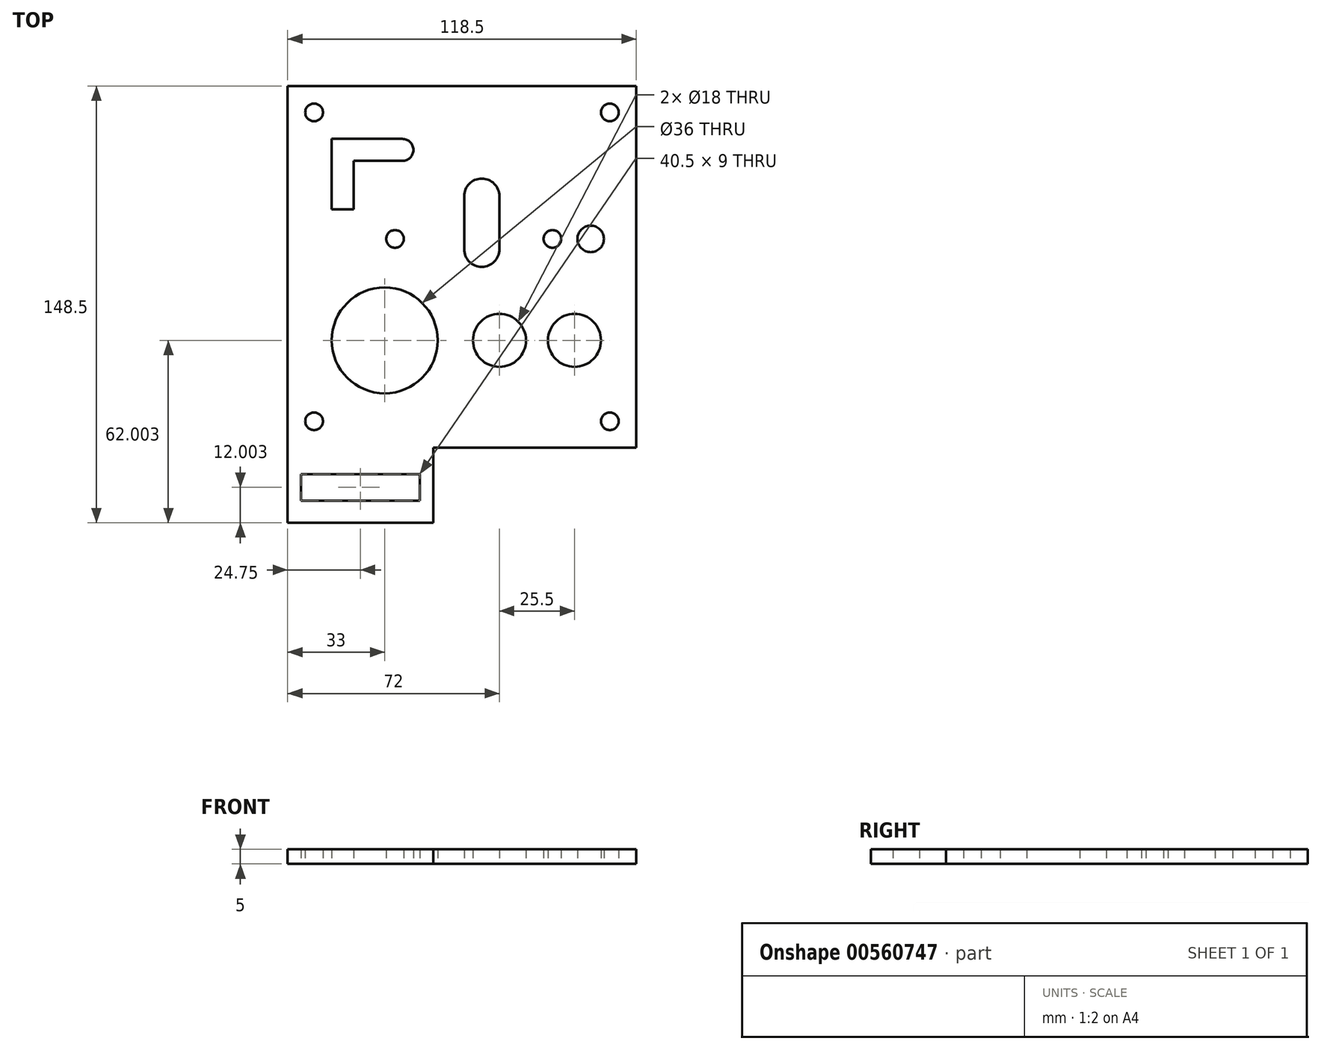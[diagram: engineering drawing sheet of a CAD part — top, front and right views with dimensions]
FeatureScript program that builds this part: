
annotation { "Feature Type Name" : "Feature", "Feature Type Description" : "" }
export const myFeature = defineFeature(function(context is Context, id is Id, definition is map)
    precondition{}
    {
        {
            var Q0;
            Q0=qCreatedBy(makeId("Top.planeOp"),FACE);
            var sketch = newSketch(context, id + "F0", { "sketchPlane" : qUnion([Q0])});
            skLineSegment(sketch, "E0", {"start": v(-66, 54.18) * mm, "end": v(52.5, 54.18) * mm});
            skLineSegment(sketch, "E1", {"start": v(52.5, 54.18) * mm, "end": v(52.5, -68.82) * mm});
            skLineSegment(sketch, "E2", {"start": v(-66, 54.18) * mm, "end": v(-66, -68.82) * mm});
            skLineSegment(sketch, "E3", {"start": v(-16.5, -68.82) * mm, "end": v(52.5, -68.82) * mm});
            skLineSegment(sketch, "E4", {"start": v(-66, 54.18) * mm, "end": v(-66, -94.32) * mm});
            skLineSegment(sketch, "E5", {"start": v(-66, -94.32) * mm, "end": v(-16.5, -94.32) * mm});
            skLineSegment(sketch, "E6", {"start": v(-16.5, -94.32) * mm, "end": v(-16.5, -68.82) * mm});
            skCircle(sketch, "E7", {"center": v(-57, 45.18) * mm, "radius": 3 * mm});
            skCircle(sketch, "E8", {"center": v(43.5, 45.18) * mm, "radius": 3 * mm});
            skCircle(sketch, "E9", {"center": v(43.5, -59.82) * mm, "radius": 3 * mm});
            skCircle(sketch, "E10", {"center": v(-57, -59.82) * mm, "radius": 3 * mm});
            skLineSegment(sketch, "E11.bottom", {"start": v(-61.5, -77.82) * mm, "end": v(-52.5, -77.82) * mm});
            skLineSegment(sketch, "E11.top", {"start": v(-61.5, -86.82) * mm, "end": v(-52.5, -86.82) * mm});
            skLineSegment(sketch, "E11.left", {"start": v(-61.5, -77.82) * mm, "end": v(-61.5, -86.82) * mm});
            skLineSegment(sketch, "E11.right", {"start": v(-52.5, -77.82) * mm, "end": v(-52.5, -86.82) * mm});
            skLineSegment(sketch, "E12.bottom", {"start": v(-45, -77.82) * mm, "end": v(-36, -77.82) * mm});
            skLineSegment(sketch, "E12.top", {"start": v(-45, -86.82) * mm, "end": v(-36, -86.82) * mm});
            skLineSegment(sketch, "E12.left", {"start": v(-45, -77.82) * mm, "end": v(-45, -86.82) * mm});
            skLineSegment(sketch, "E12.right", {"start": v(-36, -77.82) * mm, "end": v(-36, -86.82) * mm});
            skLineSegment(sketch, "E13.bottom", {"start": v(-30, -77.82) * mm, "end": v(-21, -77.82) * mm});
            skLineSegment(sketch, "E13.top", {"start": v(-30, -86.82) * mm, "end": v(-21, -86.82) * mm});
            skLineSegment(sketch, "E13.left", {"start": v(-30, -77.82) * mm, "end": v(-30, -86.82) * mm});
            skLineSegment(sketch, "E13.right", {"start": v(-21, -77.82) * mm, "end": v(-21, -86.82) * mm});
            skLineSegment(sketch, "E14", {"start": v(-61.5, -77.82) * mm, "end": v(-21, -77.82) * mm});
            skLineSegment(sketch, "E15", {"start": v(-61.5, -86.82) * mm, "end": v(-21, -86.82) * mm});
            skLineSegment(sketch, "E16", {"start": v(-51, 36.18) * mm, "end": v(-51, 12.18) * mm});
            skLineSegment(sketch, "E17", {"start": v(-51, 12.18) * mm, "end": v(-51, 36.18) * mm});
            skLineSegment(sketch, "E18", {"start": v(-51, 36.18) * mm, "end": v(-27, 36.18) * mm});
            skLineSegment(sketch, "E19", {"start": v(-51, 12.18) * mm, "end": v(-43.5, 12.18) * mm});
            skLineSegment(sketch, "E20", {"start": v(-43.5, 12.18) * mm, "end": v(-43.5, 28.68) * mm});
            skLineSegment(sketch, "E21", {"start": v(-43.5, 28.68) * mm, "end": v(-27, 28.68) * mm});
            skCircle(sketch, "E22", {"center": v(31.5, -32.32) * mm, "radius": 9 * mm});
            skCircle(sketch, "E23", {"center": v(6, -32.32) * mm, "radius": 9 * mm});
            skCircle(sketch, "E24", {"center": v(-33, -32.32) * mm, "radius": 18 * mm});
            skArc(sketch, "E25", {"start": v(-27, 28.68) * mm, "mid": v(-23.25, 32.43) * mm, "end": v(-27, 36.18) * mm});
            skLineSegment(sketch, "E26", {"start": v(-6, 16.68) * mm, "end": v(-6, -1.32) * mm});
            skLineSegment(sketch, "E27", {"start": v(6, -1.32) * mm, "end": v(6, 16.68) * mm});
            skArc(sketch, "E28", {"start": v(6, 16.68) * mm, "mid": v(0, 22.68) * mm, "end": v(-6, 16.68) * mm});
            skArc(sketch, "E29", {"start": v(-6, -1.32) * mm, "mid": v(0, -7.32) * mm, "end": v(6, -1.32) * mm});
            skCircle(sketch, "E30", {"center": v(37, 2.18) * mm, "radius": 4.5 * mm});
            skCircle(sketch, "E31", {"center": v(24, 2.18) * mm, "radius": 3 * mm});
            skCircle(sketch, "E32", {"center": v(-29.49, 2.18) * mm, "radius": 3 * mm});
            skSolve(sketch);
        }
        {
            var Q0;
            Q0 = qSketchRegion(id + "F0", true);
            extrude(context, id + "F1", {"entities" : qUnion([Q0]), "depth" : 5 * mm, "offsetDistance" : 25 * mm});
        }
    });
